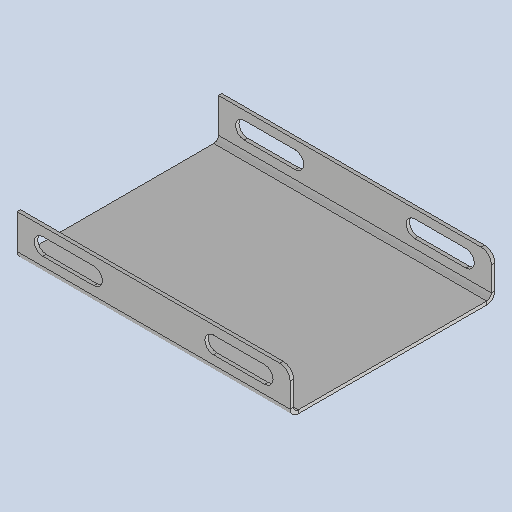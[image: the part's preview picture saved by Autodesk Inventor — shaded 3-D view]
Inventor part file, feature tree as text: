
AUTODESK INVENTOR PART (.ipt)
format: ipt  version: 2025 (Build 290162010, 162A)  size: 333,312 bytes
history: native  units: mm
features: other x5, sheet_metal_op x4, sketch x4, extrude x1, chamfer x1, projected_geometry x1
ambient origin geometry x8: Origin, YZ Plane, XZ Plane, XY Plane, X Axis, Y Axis, Z Axis, Center Point
bodies: Solid1 (feature_tree)
feature tree (16):
  sheet_metal_op  "Face1"
  other  "Mark1"
  other  "A-Side Definition"
  sheet_metal_op  "Flange1"
  extrude  "Extrusion1"  Depth=120.0mm
  chamfer  "Corner Round1"
  sketch  "Sketch1"  dims[d0=160.0mm d1=120.0mm]
  other  "Plate1"
  sketch  "Sketch2"  dims[d2=2.0mm]
  sketch  "Sketch3"  dims[d6=200.0mm]
  other  "Plate2"
  sheet_metal_op  "Bend1"
  sheet_metal_op  "Corner1"
  sketch  "Sketch4"  dims[d9=20.0mm d10=20.0mm d11=20.0mm d12=2.0mm d13=1.0mm d14=4.0mm d15=2.75mm d16=25.0mm d17=90.0deg d18=2.75mm d19=8.0mm d20=2.0mm d21=2.75mm d22=30.0mm d23=10.0mm d24=100.0mm d25=0.0mm d26=0.0mm d27=6.0mm]
  projected_geometry  "Projected Loop1"
  other  "Definition1"
